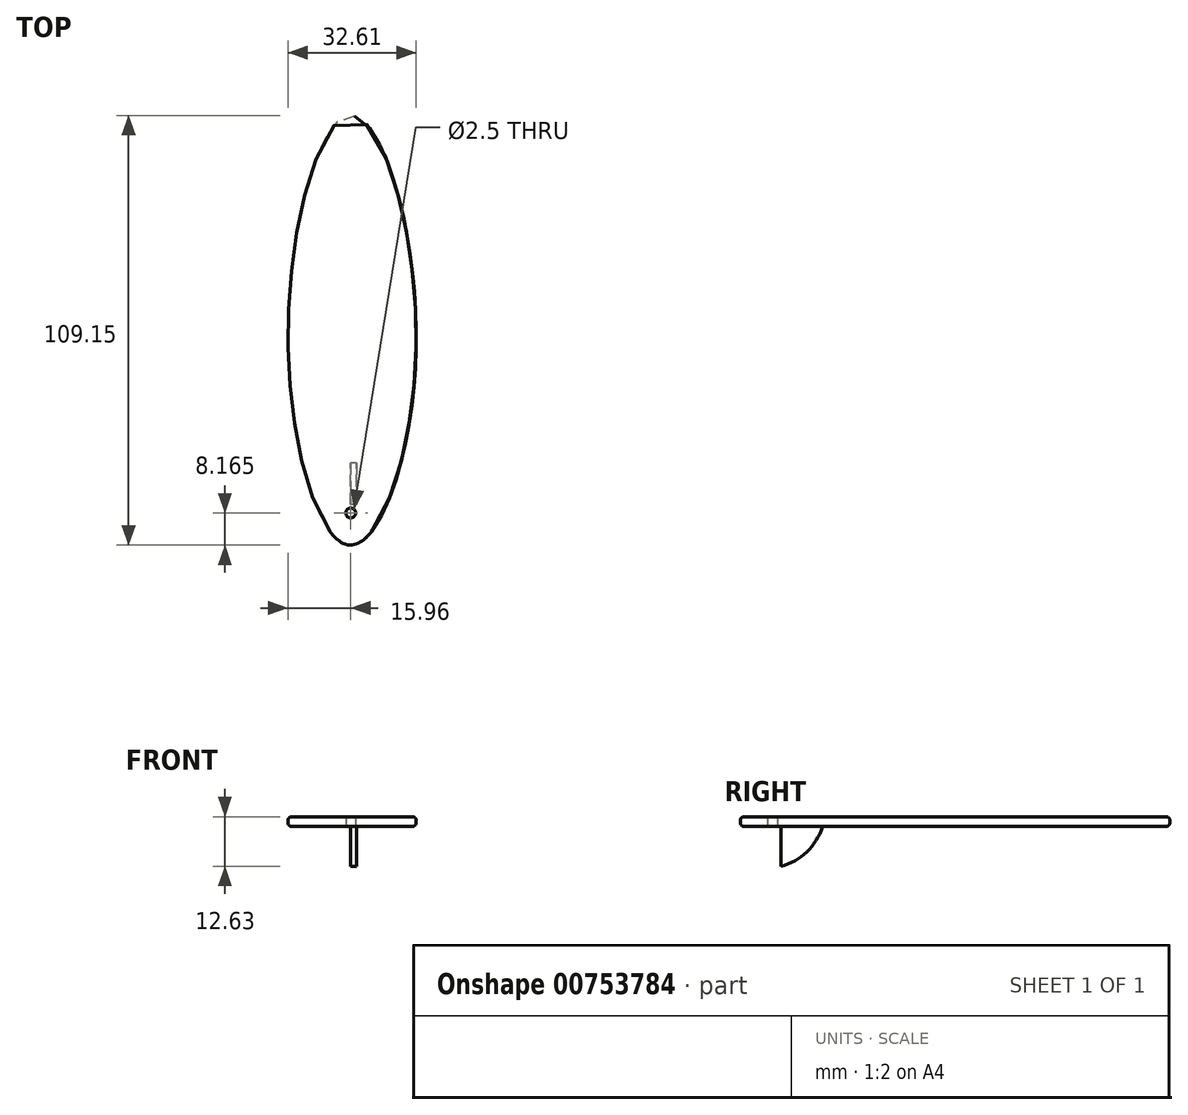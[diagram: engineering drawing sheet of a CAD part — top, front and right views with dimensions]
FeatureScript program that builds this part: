
annotation { "Feature Type Name" : "Feature", "Feature Type Description" : "" }
export const myFeature = defineFeature(function(context is Context, id is Id, definition is map)
    precondition{}
    {
        {
            var Q0;
            Q0=qCreatedBy(makeId("Top.planeOp"),FACE);
            var sketch = newSketch(context, id + "F0", { "sketchPlane" : qUnion([Q0])});
            skPoint(sketch, "E0.middle", {"position": v(0, 0) * mm});
            skFitSpline(sketch, "E1", {"points": [v(-15.88, 0) * mm, v(0, 58.03) * mm, v(16.71, 0) * mm, v(0, -51.12) * mm, v(-15.88, 0) * mm]});
            skLineSegment(sketch, "E2", {"start": v(-5.21, -47.67) * mm, "end": v(5.35, -47.67) * mm});
            skLineSegment(sketch, "E3.filletArc", {"start": v(0.02, 58.03) * mm, "end": v(0.02, 58.03) * mm});
            skPoint(sketch, "E4", {"position": v(0.07, -42.95) * mm});
            skPoint(sketch, "E4.positionSnap0", {"position": v(0.07, -47.67) * mm});
            skSolve(sketch);
        }
        {
            var Q0;
            Q0 = qSketchRegion(id + "F0", true);
            extrude(context, id + "F1", {"entities" : qUnion([Q0]), "depth" : 2.5 * mm, "offsetDistance" : 25 * mm});
        }
        {
            var Q0;
            Q0=makeQuery(id+"F1.opExtrude","CAP_EDGE",EDGE,{"disambiguationData":[OSD([sQuery(id+"F0.wireOp",EDGE,"gqBxG7Yk-uvB9-AJGW-xGMM-G8XAwIh3QYwm")])],"isStart":true});
            var Q1;
            Q1=makeQuery(id+"F1.opExtrude","CAP_EDGE",EDGE,{"disambiguationData":[OSD([sQuery(id+"F0.wireOp",EDGE,"YQDhCsJO-zbkm-UiPe-UXZ4-SJuvBBlKikjL")])],"isStart":true});
            var Q2;
            Q2=makeQuery(id+"F1.opExtrude","CAP_EDGE",EDGE,{"disambiguationData":[OSD([sQuery(id+"F0.wireOp",EDGE,"E1")])],"isStart":true});
            var Q3;
            Q3=makeQuery(id+"F1.opExtrude","CAP_EDGE",EDGE,{"disambiguationData":[OSD([sQuery(id+"F0.wireOp",EDGE,"E1")])],"isStart":true});
            var Q4;
            Q4=makeQuery(id+"F1.opExtrude","CAP_EDGE",EDGE,{"disambiguationData":[OSD([sQuery(id+"F0.wireOp",EDGE,"E2")])],"isStart":true});
            var Q5;
            Q5=makeQuery(id+"F1.opExtrude","CAP_EDGE",EDGE,{"disambiguationData":[OSD([sQuery(id+"F0.wireOp",EDGE,"E1")])],"isStart":false});
            var Q6;
            Q6=makeQuery(id+"F1.opExtrude","CAP_EDGE",EDGE,{"disambiguationData":[OSD([sQuery(id+"F0.wireOp",EDGE,"YQDhCsJO-zbkm-UiPe-UXZ4-SJuvBBlKikjL")])],"isStart":false});
            var Q7;
            Q7=makeQuery(id+"F1.opExtrude","CAP_EDGE",EDGE,{"disambiguationData":[OSD([sQuery(id+"F0.wireOp",EDGE,"gqBxG7Yk-uvB9-AJGW-xGMM-G8XAwIh3QYwm")])],"isStart":false});
            var Q8;
            Q8=makeQuery(id+"F1.opExtrude","CAP_EDGE",EDGE,{"disambiguationData":[OSD([sQuery(id+"F0.wireOp",EDGE,"E1")])],"isStart":false});
            var Q9;
            Q9=makeQuery(id+"F1.opExtrude","CAP_FACE",FACE,{"disambiguationData":[OSD([sQuery(id+"F0.wireOp",EDGE,"E1"),sQuery(id+"F0.wireOp",EDGE,"E2"),sQuery(id+"F0.wireOp",EDGE,"YQDhCsJO-zbkm-UiPe-UXZ4-SJuvBBlKikjL"),sQuery(id+"F0.wireOp",EDGE,"gqBxG7Yk-uvB9-AJGW-xGMM-G8XAwIh3QYwm"),sQuery(id+"F0.wireOp",EDGE,"E1")])],"isStart":true});
            fillet(context, id + "F2", {"entities" : qUnion([Q0, Q1, Q2, Q3, Q4, Q5, Q6, Q7, Q8, Q9]), "radius" : 1 * mm, "tangentPropagation" : true, "allowEdgeOverflow" : false});
        }
        {
            var Q0;
            Q0=qCreatedBy(makeId("Right.planeOp"),FACE);
            var sketch = newSketch(context, id + "F3", { "sketchPlane" : qUnion([Q0])});
            skLineSegment(sketch, "E5.bottom", {"start": v(-30.23, 0) * mm, "end": v(-40.84, 0) * mm});
            skLineSegment(sketch, "E5.top", {"start": v(-30.23, -10.6) * mm, "end": v(-40.84, -10.6) * mm});
            skLineSegment(sketch, "E5.left", {"start": v(-30.23, 0) * mm, "end": v(-30.23, -10.6) * mm});
            skLineSegment(sketch, "E5.right", {"start": v(-40.84, 0) * mm, "end": v(-40.84, -10.6) * mm});
            skSolve(sketch);
        }
        {
            var Q0;
            Q0 = qSketchRegion(id + "F3", true);
            extrude(context, id + "F4", {"entities" : qUnion([Q0]), "operationType" : NewBodyOperationType.ADD, "depth" : 1.5 * mm, "offsetDistance" : 25 * mm});
        }
        {
            var Q0;
            Q0=makeQuery(id+"F4.opExtrude","SWEPT_EDGE",EDGE,{"disambiguationData":[OSD([sQuery(id+"F3.wireOp",EDGE,"E5.top"),sQuery(id+"F3.wireOp",EDGE,"E5.left")])]});
            fillet(context, id + "F5", {"entities" : qUnion([Q0]), "radius" : 15 * mm, "tangentPropagation" : true, "allowEdgeOverflow" : false});
        }
        {
            var Q0;
            Q0=sQuery(id+"F0.wireOp",VERTEX,"E4");
            var Q1;
            Q1=makeQuery(id+"F1.opExtrude","SWEPT_BODY",BODY,{"disambiguationData":[OSD([sQuery(id+"F0.wireOp",EDGE,"E1"),sQuery(id+"F0.wireOp",EDGE,"E2"),sQuery(id+"F0.wireOp",EDGE,"E1")])]});
            hole(context, id + "F6", {"style" : HoleStyle.SIMPLE, "endStyle" : HoleEndStyle.THROUGH, "oppositeDirection" : true, "holeDiameter" : 2.5 * mm, "majorDiameter" : 5 * mm, "isTappedThrough" : true, "tappedDepth" : 12 * mm, "tapClearance" : 3, "locations" : qUnion([Q0]), "scope" : qUnion([Q1])});
        }
    });
